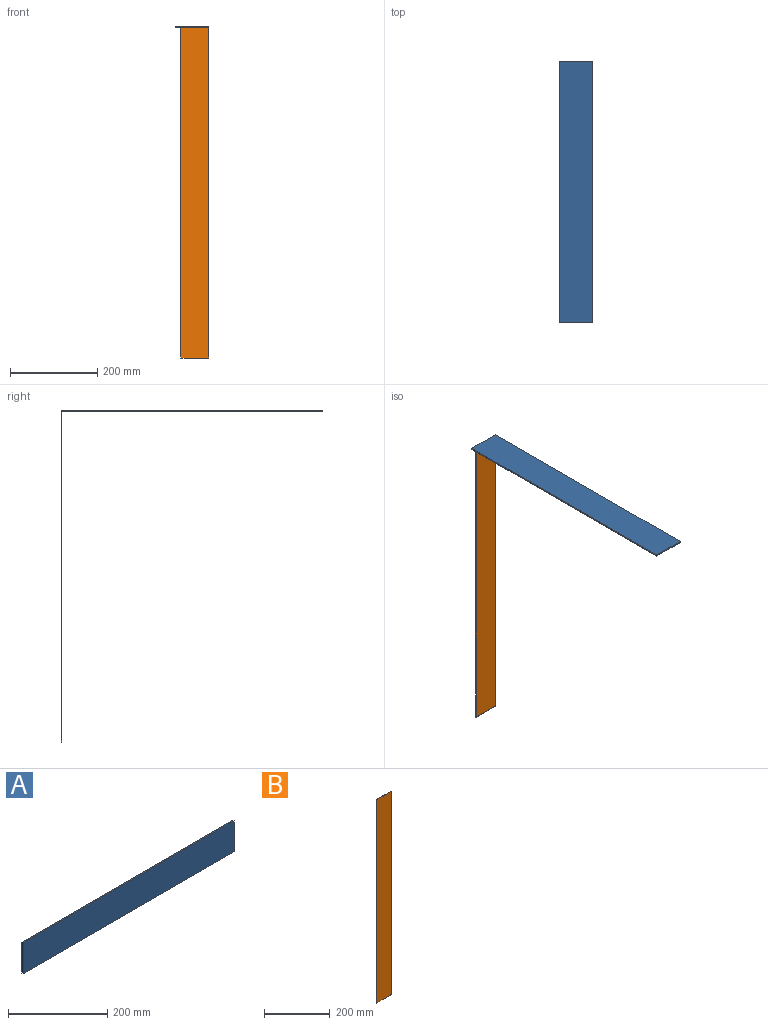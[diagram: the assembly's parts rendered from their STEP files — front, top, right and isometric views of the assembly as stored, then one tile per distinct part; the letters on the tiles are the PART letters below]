
ASSEMBLY  parts=2 mates=1
PART A: 6 faces, bbox 600.1x3.2x76.2 mm
  f0: plane 600.08x3.18mm, normal (0,0,1), area 1905.2mm2, adj f1,f3,f4,f5
  f1: plane 76.2x3.18mm, normal (-1,0,0), area 241.9mm2, adj f0,f2,f4,f5
  f2: plane 600.08x3.18mm, normal (0,0,-1), area 1905.2mm2, adj f1,f3,f4,f5
  f3: plane 76.2x3.18mm, normal (1,0,0), area 241.9mm2, adj f0,f2,f4,f5
  f4: plane 600.08x76.2mm, normal (0,1,0), area 45725.7mm2, adj f0,f1,f2,f3
  f5: plane 600.08x76.2mm, normal (0,-1,0), area 45725.7mm2, adj f0,f1,f2,f3
PART B: 6 faces, bbox 63.5x1.2x758.8 mm
  f0: plane 758.83x1.22mm, normal (-1,0,0), area 925.2mm2, adj f1,f3,f4,f5
  f1: plane 63.5x1.22mm, normal (0,0,-1), area 77.4mm2, adj f0,f2,f4,f5
  f2: plane 758.83x1.22mm, normal (1,0,0), area 925.2mm2, adj f1,f3,f4,f5
  f3: plane 63.5x1.22mm, normal (0,0,1), area 77.4mm2, adj f0,f2,f4,f5
  f4: plane 758.83x63.5mm, normal (0,-1,0), area 48185.4mm2, adj f0,f1,f2,f3
  f5: plane 758.83x63.5mm, normal (0,1,0), area 48185.4mm2, adj f0,f1,f2,f3
PLACE A rot(axis=(0.58,0.58,0.58),120deg) t=(31.75,-600.21,381.71)mm
PLACE B t=(-31.75,-0.13,-377.12)mm
MATE ball A.f0 <-> B.f2  axis (1,0,0) through (31.75,-0.13,381.71)mm
